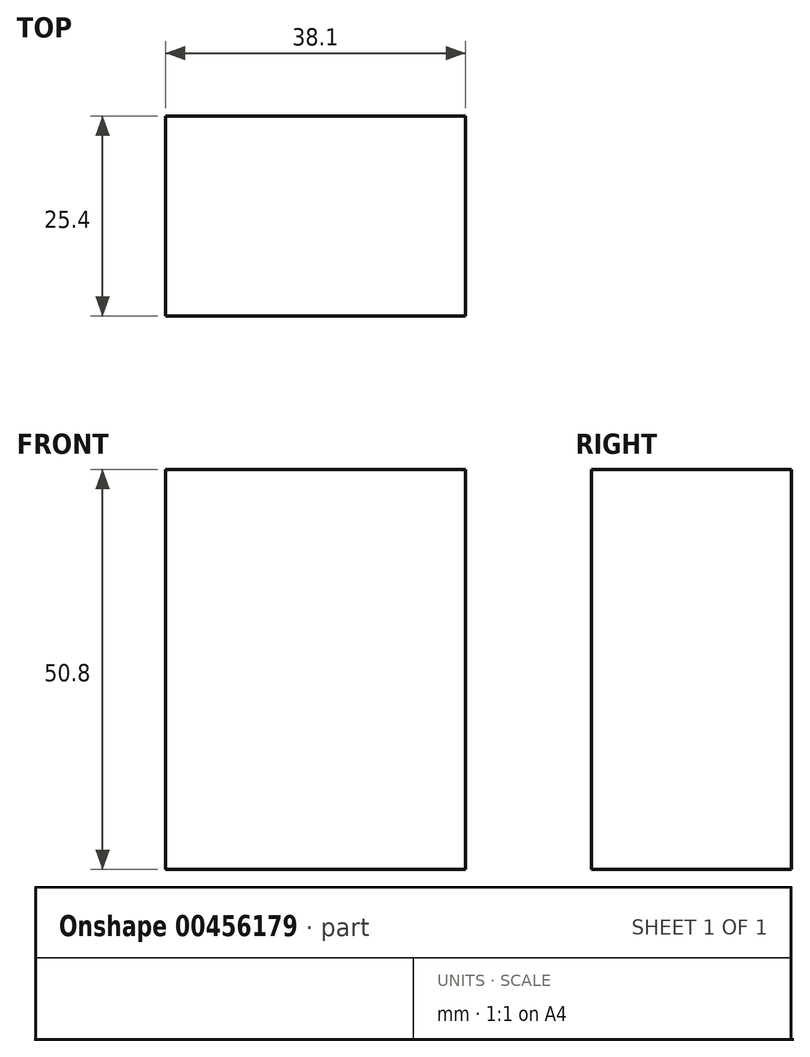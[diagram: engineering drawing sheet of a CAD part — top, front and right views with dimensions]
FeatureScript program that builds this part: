
annotation { "Feature Type Name" : "Feature", "Feature Type Description" : "" }
export const myFeature = defineFeature(function(context is Context, id is Id, definition is map)
    precondition{}
    {
        {
            var Q0;
            Q0=qCreatedBy(makeId("Top.planeOp"),FACE);
            var sketch = newSketch(context, id + "F0", { "sketchPlane" : qUnion([Q0])});
            skLineSegment(sketch, "E0.bottom", {"start": v(0, 0) * mm, "end": v(25.4, 0) * mm});
            skLineSegment(sketch, "E0.top", {"start": v(0, 50.8) * mm, "end": v(25.4, 50.8) * mm});
            skLineSegment(sketch, "E0.left", {"start": v(0, 0) * mm, "end": v(0, 50.8) * mm});
            skLineSegment(sketch, "E0.right", {"start": v(25.4, 0) * mm, "end": v(25.4, 50.8) * mm});
            skSolve(sketch);
        }
        {
            var Q0;
            Q0=makeQuery(id+"F0.imprint","IMPRINT",FACE,{"disambiguationData":[TD([[makeQuery(id+"F0.imprint","IMPRINT",EDGE,{"derivedFrom":sQuery(id+"F0.wireOp",EDGE,"E0.bottom")}),1.0]])]});
            extrude(context, id + "F1", {"entities" : qUnion([Q0]), "depth" : 25.4 * mm});
        }
        {
            var Q0;
            Q0=makeQuery(id+"F1.opExtrude","SWEPT_BODY",BODY,{"disambiguationData":[OSD([sQuery(id+"F0.wireOp",EDGE,"E0.bottom"),sQuery(id+"F0.wireOp",EDGE,"E0.top"),sQuery(id+"F0.wireOp",EDGE,"E0.left"),sQuery(id+"F0.wireOp",EDGE,"E0.right")])]});
            var Q1;
            Q1=makeQuery(id+"F1.opExtrude","CAP_EDGE",EDGE,{"disambiguationData":[OSD([sQuery(id+"F0.wireOp",EDGE,"E0.bottom")])],"isStart":true});
            transform(context, id + "F2", {"entities" : qUnion([Q0]), "transformType" : TransformType.ROTATION, "transformAxis" : qUnion([Q1]), "angle" : 90 * degree, "makeCopy" : false});
        }
        {
            var Q0;
            Q0=makeQuery(id+"F1.opExtrude","SWEPT_FACE",FACE,{"disambiguationData":[OSD([sQuery(id+"F0.wireOp",EDGE,"E0.left")])]});
            extrude(context, id + "F3", {"entities" : qUnion([Q0]), "operationType" : NewBodyOperationType.ADD, "depth" : 12.7 * mm});
        }
        {
            var Q0;
            Q0=qCreatedBy(makeId("Front.planeOp"),FACE);
            var sketch = newSketch(context, id + "F4", { "sketchPlane" : qUnion([Q0])});
            skCircle(sketch, "E1", {"center": v(4.64, 51.4) * mm, "radius": 6.35 * mm});
            skSolve(sketch);
        }
        {
            var Q0;
            Q0=makeQuery(id+"F1.opExtrude","SWEPT_BODY",BODY,{"disambiguationData":[OSD([sQuery(id+"F0.wireOp",EDGE,"E0.bottom"),sQuery(id+"F0.wireOp",EDGE,"E0.top"),sQuery(id+"F0.wireOp",EDGE,"E0.left"),sQuery(id+"F0.wireOp",EDGE,"E0.right")])]});
            transform(context, id + "F5", {"entities" : qUnion([Q0]), "transformType" : TransformType.TRANSLATION_3D, "dx" : -6.35 * mm, "dy" : 0 * mm, "dz" : 0 * mm, "makeCopy" : false});
        }
        {
            var Q0;
            Q0=makeQuery(id+"F4.imprint","IMPRINT",FACE,{"disambiguationData":[TD([[makeQuery(id+"F4.imprint","IMPRINT",EDGE,{"derivedFrom":sQuery(id+"F4.wireOp",EDGE,"E1")}),1.0]])]});
            var Q1;
            Q1=sQuery(id+"F4.wireOp",EDGE,"E1");
            extrude(context, id + "F6", {"entities" : qUnion([Q0]), "bodyType" : ToolBodyType.SURFACE, "operationType" : NewBodyOperationType.INTERSECT, "surfaceEntities" : qUnion([Q1]), "depth" : 25.4 * mm});
        }
    });
